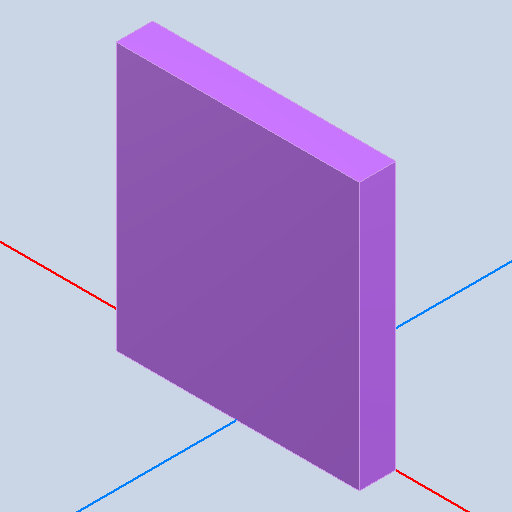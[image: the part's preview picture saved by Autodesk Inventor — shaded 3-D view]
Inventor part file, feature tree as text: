
AUTODESK INVENTOR PART (.ipt)
format: ipt  version: 2022 (Build 260153000, 153)  size: 91,648 bytes
history: native  units: mm
features: other x2, extrude x1
ambient origin geometry x8: Origin, YZ Plane, XZ Plane, XY Plane, X Axis, Y Axis, Z Axis, Center Point
bodies: Body1 (feature_tree)
feature tree (3):
  other  "Твердое тело1"
  extrude  "Выдавливание1"  Depth=1.0mm TaperAngle=0.0deg
  other  "SOT223, U3_SOT223_16"
